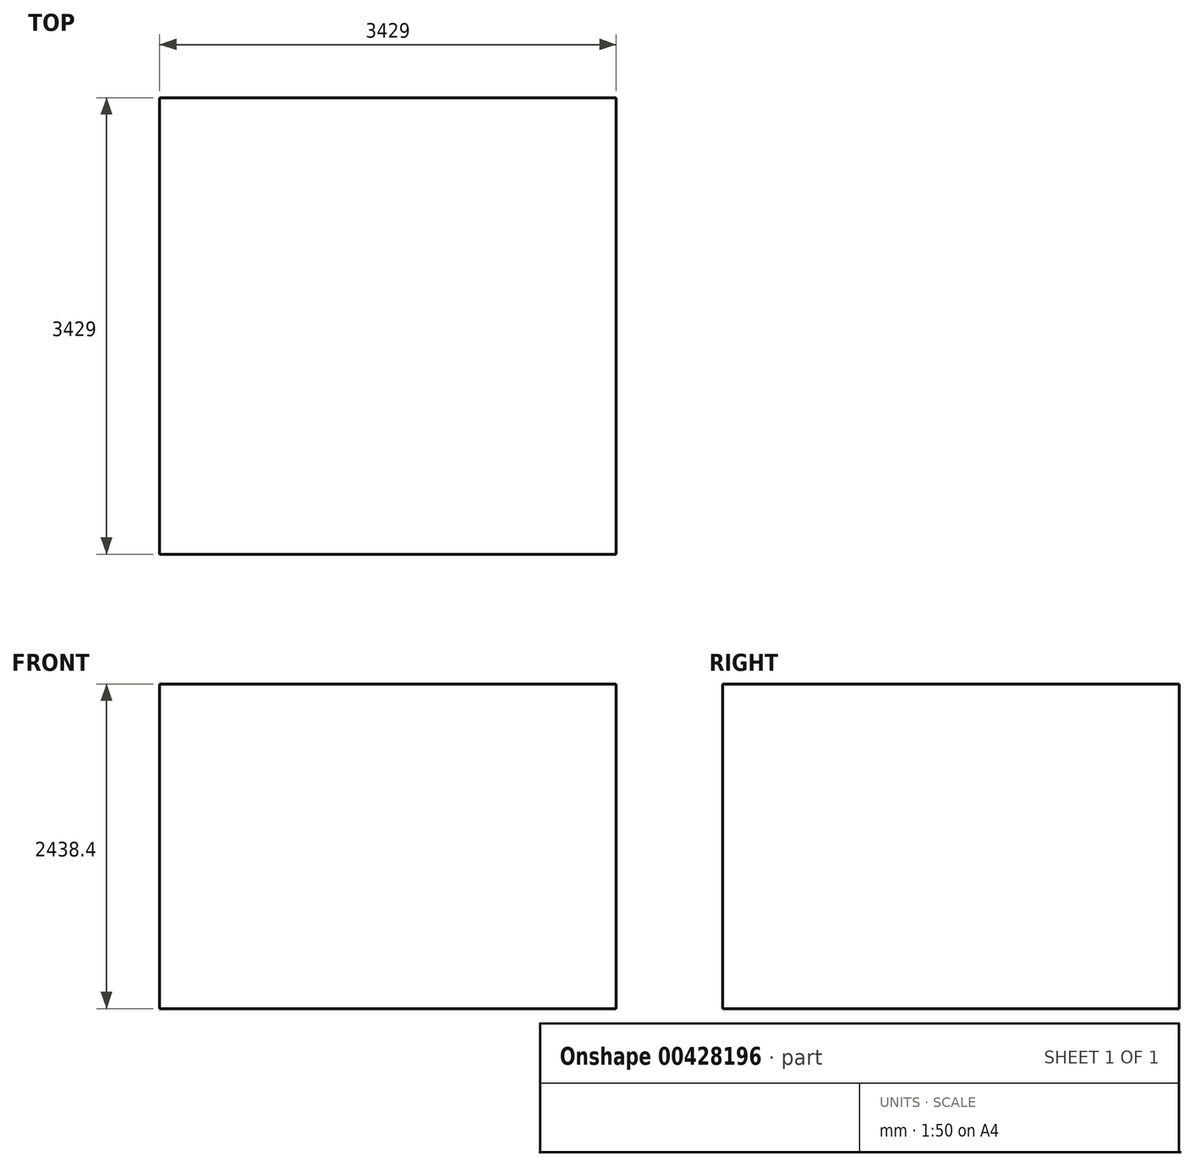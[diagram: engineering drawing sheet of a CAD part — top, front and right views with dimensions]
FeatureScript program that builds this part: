
annotation { "Feature Type Name" : "Feature", "Feature Type Description" : "" }
export const myFeature = defineFeature(function(context is Context, id is Id, definition is map)
    precondition{}
    {
        {
            var Q0;
            Q0=qCreatedBy(makeId("Top.planeOp"),FACE);
            var sketch = newSketch(context, id + "F0", { "sketchPlane" : qUnion([Q0])});
            skLineSegment(sketch, "E0.bottom", {"start": v(1714.5, -1714.5) * mm, "end": v(-1714.5, -1714.5) * mm});
            skLineSegment(sketch, "E0.top", {"start": v(1714.5, 1714.5) * mm, "end": v(-1714.5, 1714.5) * mm});
            skLineSegment(sketch, "E0.left", {"start": v(1714.5, -1714.5) * mm, "end": v(1714.5, 1714.5) * mm});
            skLineSegment(sketch, "E0.right", {"start": v(-1714.5, -1714.5) * mm, "end": v(-1714.5, 1714.5) * mm});
            skPoint(sketch, "E0.middle", {"position": v(0, 0) * mm});
            skSolve(sketch);
        }
        {
            var Q0;
            Q0=makeQuery(id+"F0.imprint","IMPRINT",FACE,{"disambiguationData":[TD([[makeQuery(id+"F0.imprint","IMPRINT",EDGE,{"derivedFrom":sQuery(id+"F0.wireOp",EDGE,"E0.bottom")}),-1.0]])]});
            extrude(context, id + "F1", {"entities" : qUnion([Q0]), "depth" : 2438.4 * mm});
        }
    });
